# Revit family: Intono 3.2
name_source: partatom
category: Lighting Fixtures
revit_build: Autodesk Revit 2017 (Build: 20170419_0315(x64)
units: mm (PartAtom-declared; Revit-internal decimal feet)

## family parameters
Cut with Voids When Loaded = Yes
Host = Face
Light Source = Yes
Part Type = Normal
Room Calculation Point = Yes
Round Connector Dimension = Use Diameter
Shared = No

## types (7) — shared parameters
Apparent Load = 0 VA
Apparent Load Phase 1 = 20 W
Body = L&L_Die-cast aluminium
CRI = 90 (also available: CRI 80 - ref. URL Technical sheet)
Code = -
Color Filter = 16777215
Control system = 1-10V, ON/OFF
Cutout dimensions = -
Default Elevation = 1219 mm
Delivered lumen output = 837 lm (3000K, 15°, CRI 80) per beam, 696 lm (3000K, 15°, CRI 90) per beam
Description = Wall mounted for outdoor applications
Dimming Lamp Color Temperature Shift = <None>
Emit from Line Length = 610 mm
Energy efficiency class = A A+ A++
Features = -
Height mm = 240 mm  [stored 0.787402 ft]
IP = IP65
LED Colour = 3000K (also available: 2700K and 4000K - ref. URL Technical sheet)
Length mm = 80 mm  [stored 0.262467 ft]
Lens = L&L_Tempered extra-clear glass
Lumen output at source = 988 lm (3000K, CRI 80) per beam, 822 lm (3000K, CRI 90) per beam
Manufacturer = L&L Luce&Light
Material = body in die-cast aluminium, screen in black-serigraphed, tempered, transparent extra-clear glass
Model = Intono 3.2
Mounting = surface mounted (wall)
No. and type of led = 2 high power density COB LEDs, 2-step MacAdam, 50 000h L95 B10 (Ta 25°C)
Notes = version compatible with Google Home or Amazon Echo available on request for voice command control; DALI version available on request
Power = 20W
Power cables = -
Power supply = 230Vac
Power supply unit = built in
Screen = L&L_Black-serigraphed
Tilt Angle = 180.00°
Tiltable = -
URL = https://www.lucelight.it
URL Accessories and power supply units = https://www.lucelight.it
URL Catalogue = https://www.lucelight.it
URL DXF = https://www.lucelight.it
URL Description = https://www.lucelight.it
URL General code = https://www.lucelight.it
URL IES Photometric file = https://www.lucelight.it
URL Image = https://www.lucelight.it
URL Technical sheet = https://www.lucelight.it
Voltage = 230 V
Weight kg = 2.20 kg
Width mm = 121 mm  [stored 0.396982 ft]
Wiring = parallel

## per-type parameters (varying)
| type | Light Source | Optics | Photometric Web File |
| Intono 3.2 LL 43° (3000K 20W 230Vac) | Intono 3.1_Light Source : L 43° | 43°+43° | INTONO 3.1 L 43° [3000K 10W 230Vac].IES |
| Intono 3.2 MM 20° (3000K 20W 230Vac) | Intono 3.1_Light Source : M 20° | 20°+20° | INTONO 3.1 M 20° [3000K 10W 230Vac].IES |
| Intono 3.2 SL 15°+43° (3000K 20W 230Vac) | Intono 3.1_Light Source : L 43° | 15°+43° | INTONO 3.1 S 15° [3000K 10W 230Vac].IES |
| Intono 3.2 SS 15° (3000K 20W 230Vac) | Intono 3.1_Light Source : S 15° | 15°+15° | INTONO 3.1 S 15° [3000K 10W 230Vac].IES |
| Intono 3.2 WA (3000K 20W 230Vac) | Intono 3.1_Light Source : A | wall grazing + asymmetrical | INTONO 3.1 W [3000K 10W 230Vac].IES |
| Intono 3.2 WW (3000K 20W 230Vac) | Intono 3.1_Light Source : W | wall grazing + wall grazing | INTONO 3.1 W [3000K 10W 230Vac].IES |
| Intono 3.2 ZW (3000K 20W 230Vac) | Intono 3.1_Light Source : W | asymmetrical 11°+ wall grazing | INTONO 3.1 Z 11° [3000K 10W 230Vac].IES |

note: [stored X ft] marks values corroborated as IEEE doubles in the binary element streams (Revit-internal decimal feet)

## geometry (parser evidence)
native form markers: Blend x2, Sweep x4
no freeform markers — native parametric forms only
